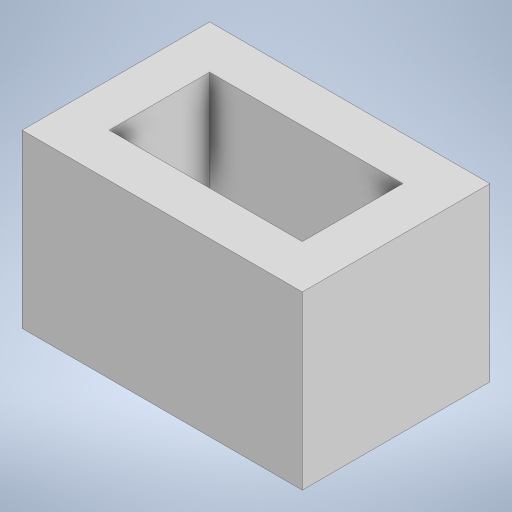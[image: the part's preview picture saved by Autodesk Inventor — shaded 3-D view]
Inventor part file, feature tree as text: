
AUTODESK INVENTOR PART (.ipt)
format: ipt  version: 2023.5 (Build 275446000, 446)  size: 192,000 bytes
history: native  units: in
note: dims shown in document units (in); Inventor stores cm internally (conversion verified against a paired STEP export)
features: extrude x3, sketch x3
ambient origin geometry x8: Origin, YZ Plane, XZ Plane, XY Plane, X Axis, Y Axis, Z Axis, Center Point
bodies: Solid1 (feature_tree)
feature tree (6):
  extrude  "Extrusion1"  Depth=0.2717in
  extrude  "Extrusion2"  Depth=0.1181in
  extrude  "Extrusion3"  Depth=0.1181in
  sketch  "Sketch1"  dims[d0=0.5224in d1=0.2717in]
  sketch  "Sketch2"  dims[d2=0.1181in d3=0.1181in]
  sketch  "Sketch3"  dims[d4=0.1181in d5=0.1181in d6=0.3465in d7=0.0in d8=0.1181in d9=0.0in d10=0.3268in d11=0.1181in d12=0.0in]
